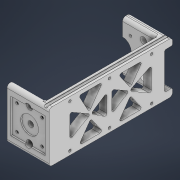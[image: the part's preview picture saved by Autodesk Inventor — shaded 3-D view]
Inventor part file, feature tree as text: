
AUTODESK INVENTOR PART (.ipt)
format: ipt  version: 2022 (Build 260153000, 153)  size: 594,432 bytes
history: native  units: mm
features: sketch x23, extrude x22, fillet x5, chamfer x2, plane x1
ambient origin geometry x8: Origin, YZ Plane, XZ Plane, XY Plane, X Axis, Y Axis, Z Axis, Center Point
bodies: Solid1 (feature_tree)
feature tree (53):
  extrude  "Extrusion1"  Depth=63.0mm
  extrude  "Extrusion2"  Depth=42.5mm
  extrude  "Extrusion3"  Depth=2.0mm TaperAngle=0.0deg
  extrude  "Extrusion4"  Depth=31.0mm
  extrude  "Extrusion6"  Depth=3.5mm
  extrude  "Extrusion7"  Depth=3.5mm
  extrude  "Extrusion8"  Depth=5.9mm
  extrude  "Extrusion9"  Depth=5.9mm
  extrude  "Extrusion11"  Depth=5.0mm TaperAngle=0.0deg
  extrude  "Extrusion12"  Depth=1.5mm TaperAngle=0.0deg
  sketch  "Sketch14"  dims[d29=7.0mm d30=54.0mm d31=0.0mm d32=20.0mm]
  extrude  "Extrusion14"  Depth=54.0mm TaperAngle=0.0deg
  fillet  "Fillet4"  Radius=20.0mm
  sketch  "Sketch16"  dims[d34=8.0mm]
  chamfer  "Chamfer2"  Distance=15.0mm
  extrude  "Extrusion15"  Depth=10.0mm TaperAngle=0.0deg
  fillet  "Fillet5"  Radius=10.0mm
  fillet  "Fillet6"  Radius=42.0mm
  extrude  "Extrusion16"  Depth=6.0mm TaperAngle=0.0deg
  extrude  "20 ml syringe (Braun)"  Depth=2.0mm
  extrude  "Extrusion21"  Depth=10.0mm TaperAngle=0.0deg
  chamfer  "Chamfer3"  Distance=3.2mm
  extrude  "Extrusion22"  Depth=1.5mm
  extrude  "Extrusion23"  Depth=1.5mm
  extrude  "Extrusion24"  Depth=1.5mm
  plane  "Work Plane1"
  extrude  "Extrusion25"  Depth=1.5mm
  extrude  "Extrusion26"  Depth=10.0mm TaperAngle=0.0deg
  fillet  "Fillet7"  Radius=21.7mm
  extrude  "Extrusion27"  Depth=10.0mm TaperAngle=0.0deg
  extrude  "Extrusion28"  Depth=1.5mm
  fillet  "Fillet8"  Radius=6.0mm
  sketch  "Sketch1"  dims[d0=52.0mm d1=63.0mm]
  sketch  "Sketch2"  dims[d2=8.0mm d3=0.0mm d4=42.5mm]
  sketch  "Sketch3"  dims[d5=42.5mm d6=2.0mm d7=0.0mm]
  sketch  "Sketch4"  dims[d8=31.0mm d9=31.0mm]
  sketch  "Sketch6"  dims[d10=3.5mm d11=3.5mm]
  sketch  "Sketch7"  dims[d12=3.5mm d13=3.5mm]
  sketch  "Sketch8"  dims[d14=4.0mm d15=0.0mm d16=5.9mm]
  sketch  "Sketch9"  dims[d17=5.9mm d18=5.9mm]
  sketch  "Sketch11"  dims[d19=5.9mm d20=5.0mm d21=0.0mm]
  sketch  "Sketch12"  dims[d26=22.1mm d27=1.5mm d28=0.0mm]
  sketch  "Sketch15"  dims[d33=20.0mm]
  sketch  "Sketch17"  dims[d35=8.0mm d36=15.0mm d37=0.0mm]
  sketch  "Sketch18"  dims[d38=10.0mm d39=145.0mm d40=0.0mm d44=10.0mm d45=42.0mm d46=0.0mm]
  sketch  "Sketch22"  dims[d47=8.1mm d48=6.0mm d49=0.0mm]
  sketch  "Sketch30"  dims[d69=20.0mm d70=0.0mm d71=2.0mm]
  sketch  "Sketch31"  dims[d75=3.4mm d76=2.0mm d77=45.0deg d78=10.0mm d79=0.0mm]
  sketch  "Sketch32"  dims[d80=4.0mm]
  sketch  "Sketch35"  dims[d81=4.0mm]
  sketch  "Sketch36"  dims[d82=20.0mm]
  sketch  "Sketch37"  dims[d84=5.0mm]
  sketch  "Sketch40"  dims[d85=5.0mm d86=3.2mm d87=3.2mm d88=20.0mm d89=3.2mm d90=3.2mm d91=10.0mm d92=0.0mm d106=21.7mm d107=10.0mm d108=0.0mm d109=5.0mm d110=6.0mm d111=48.0mm d112=8.0mm d113=15.0mm d114=23.0mm d115=3.2mm d122=15.0mm d123=15.0mm d124=30.0deg d125=15.0mm d126=15.0mm d127=90.0deg d128=60.0deg d129=15.0mm d130=180.0deg d131=15.003663mm d132=9.599311mm d133=15.0mm d134=15.0mm d135=0.0mm d136=9.599311mm d137=3.0mm d139=15.0mm d140=15.0mm d141=60.0deg d142=3.0mm d143=0.0mm d144=15.0mm d145=15.0mm d146=9.599311mm d147=15.0mm d148=15.0mm d149=0.0mm d150=9.599311mm d151=2.0mm d152=10.0mm d153=0.0mm d154=2.0mm d155=2.0mm d156=45.0deg d157=17.0mm d158=10.0mm d159=34.0mm d160=90.0deg d161=3.2mm d162=3.2mm d163=10.0mm d164=0.0mm d165=2.75mm d166=90.0deg d167=2.75mm d168=1.0mm d169=0.0mm d170=5.0mm d171=10.0mm d172=45.5mm d173=10.0mm d174=0.0mm d175=-5.0mm d176=15.0mm d177=15.5mm d178=3.5mm d179=3.5mm d180=10.0mm d181=0.0mm d182=2.75mm d183=2.75mm d184=2.75mm d185=2.5mm d186=0.0mm d187=2.0mm d188=5.9mm d189=5.9mm d191=5.9mm d192=5.9mm d194=5.0mm d195=0.0mm d196=4.0mm d197=2.0mm d198=0.0mm d199=1.5mm d200=5.9mm d201=5.9mm]
